# Revit family: Reduzierwinkel_Endabschluss für Kabelrinne_ Russia
name_source: partatom
category: Generic Models
revit_build: Autodesk Revit 2015 (Build: 20140606_1530(x64)
units: mm (PartAtom-declared; Revit-internal decimal feet)

## types (7) — shared parameters
Manufacturer = OBO Bettermann
Material = Steel, Galvanized
URL = http://www.obo-bettermann.com

## per-type parameters (varying)
| type | "B" Dimension | Article Type | GTIN | Manufacturer Art. No. | Width |
| RWEB 610 FS RU | 195 mm  [stored 0.639764 ft] | RWEB 610 FS RU | 4012196606269 | 7109611 | 16 mm  [stored 0.0524934 ft] |
| RWEB 620 FS RU | 295 mm  [stored 0.967848 ft] | RWEB 620 FS RU | 4012196606276 | 7109613 | 40 mm  [stored 0.131234 ft] |
| RWEB 615 FS RU | 245 mm  [stored 0.803806 ft] | RWEB 615 FS RU | 4012196649433 | 7109612 | 16 mm  [stored 0.0524934 ft] |
| RWEB 630 FS RU | 395 mm  [stored 1.29593 ft] | RWEB 630 FS RU | 4012196606283 | 7109615 | 40 mm  [stored 0.131234 ft] |
| RWEB 640 FS RU | 495 mm  [stored 1.62402 ft] | RWEB640 FS RU | 4012196626267 | 7109617 | 40 mm  [stored 0.131234 ft] |
| RWEB 650 FS RU | 595 mm  [stored 1.9521 ft] | RWEB 650 FS RU | 4012196626274 | 7109619 | 40 mm  [stored 0.131234 ft] |
| RWEB 660 FS RU | 695 mm  [stored 2.28018 ft] | RWEB 660 FS RU | 4012196626281 | 7109621 | 40 mm  [stored 0.131234 ft] |

note: [stored X ft] marks values corroborated as IEEE doubles in the binary element streams (Revit-internal decimal feet)

## geometry (parser evidence)
native form markers: Sweep x2
no freeform markers — native parametric forms only
